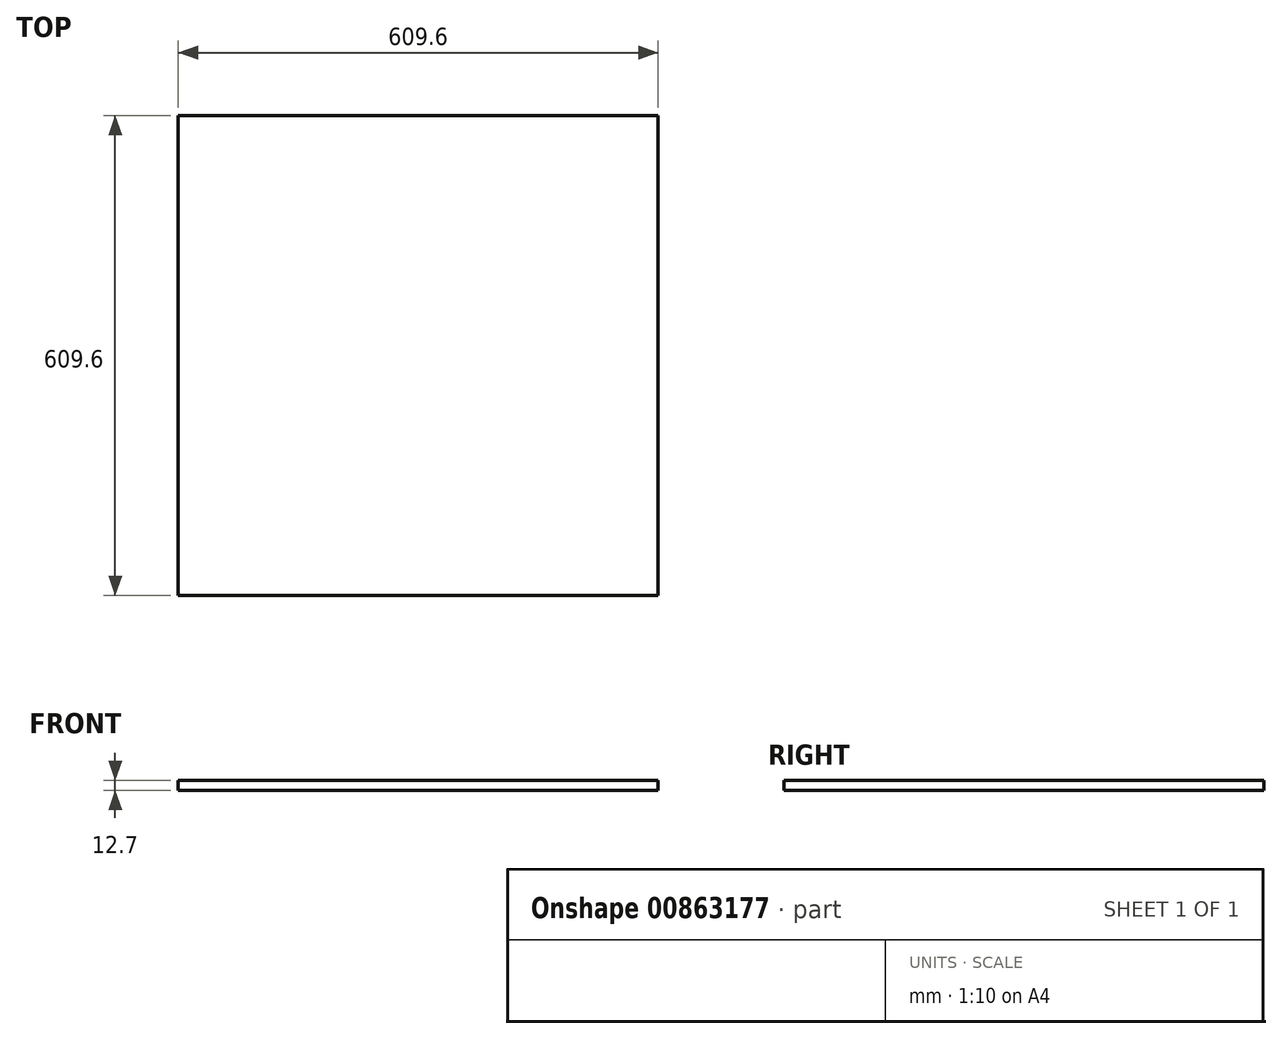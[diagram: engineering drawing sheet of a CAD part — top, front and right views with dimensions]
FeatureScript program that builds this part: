
annotation { "Feature Type Name" : "Feature", "Feature Type Description" : "" }
export const myFeature = defineFeature(function(context is Context, id is Id, definition is map)
    precondition{}
    {
        {
            var Q0;
            Q0=qCreatedBy(makeId("Top.planeOp"),FACE);
            var sketch = newSketch(context, id + "F0", { "sketchPlane" : qUnion([Q0])});
            skLineSegment(sketch, "E0.bottom", {"start": v(304.8, 304.8) * mm, "end": v(-304.8, 304.8) * mm});
            skLineSegment(sketch, "E0.top", {"start": v(304.8, -304.8) * mm, "end": v(-304.8, -304.8) * mm});
            skLineSegment(sketch, "E0.left", {"start": v(304.8, 304.8) * mm, "end": v(304.8, -304.8) * mm});
            skLineSegment(sketch, "E0.right", {"start": v(-304.8, 304.8) * mm, "end": v(-304.8, -304.8) * mm});
            skPoint(sketch, "E0.middle", {"position": v(0, 0) * mm});
            skSolve(sketch);
        }
        {
            var Q0;
            Q0=makeQuery(id+"F0.imprint","IMPRINT",FACE,{"disambiguationData":[TD([[makeQuery(id+"F0.imprint","IMPRINT",EDGE,{"derivedFrom":sQuery(id+"F0.wireOp",EDGE,"E0.bottom")}),1.0]])]});
            extrude(context, id + "F1", {"entities" : qUnion([Q0]), "depth" : 12.7 * mm, "offsetDistance" : 25.4 * mm});
        }
    });
